# Revit family: C 80 (a)
name_source: partatom
category: Equipement spécialisé
revit_build: Autodesk Revit LT 2015 (Build: 20140606_1530(x64)
units: mm (PartAtom-declared; Revit-internal decimal feet)

## types (5) — shared parameters
Apparent Power = 0 VA
Depth = 350 mm  [stored 1.14829 ft]
Description = TAMIS AUTOMATIQUES
Electrique connexion = 120 mm  [stored 0.393701 ft]
Fabricant = ROBOT COUPE
Height = 520 mm
Modèle = C 80
Phase = 1
URL = www.robot-coupe.com
Width Electrique connexion = 55 mm  [stored 0.180446 ft]
water = Connector
zero-valued in all types: Cold water supply, Cold water supply height, Used water, Waste water height

## per-type parameters (varying)
| type | Amps | Cycle | HP | Speeds (Rpm) | Volts | Weight |
| C 80    230/50/1 | 5.7 A | 50 Hz |  | 1500 | 230 V | 20.6 Kg |
| C 80    115/60/1 | 12 A | 60 Hz |  | 1500 | 115 V | 20.6 Kg |
| C 80    220/60/1 | 12 A | 60 Hz |  | 1500 | 220 V | 20.6 Kg |
| C 80    220-240/50/1 | 5.7 A | 50 Hz |  | 1500 | 220 V | 20.6 Kg |
| C 80  USA    120/60/1 | 12 A | 60 Hz | 3/4 | 1725 | 120 V | 40.8 lbs |

note: [stored X ft] marks values corroborated as IEEE doubles in the binary element streams (Revit-internal decimal feet)

## geometry (parser evidence)
native form markers: Blend x106, Sweep x5
no freeform markers — native parametric forms only
